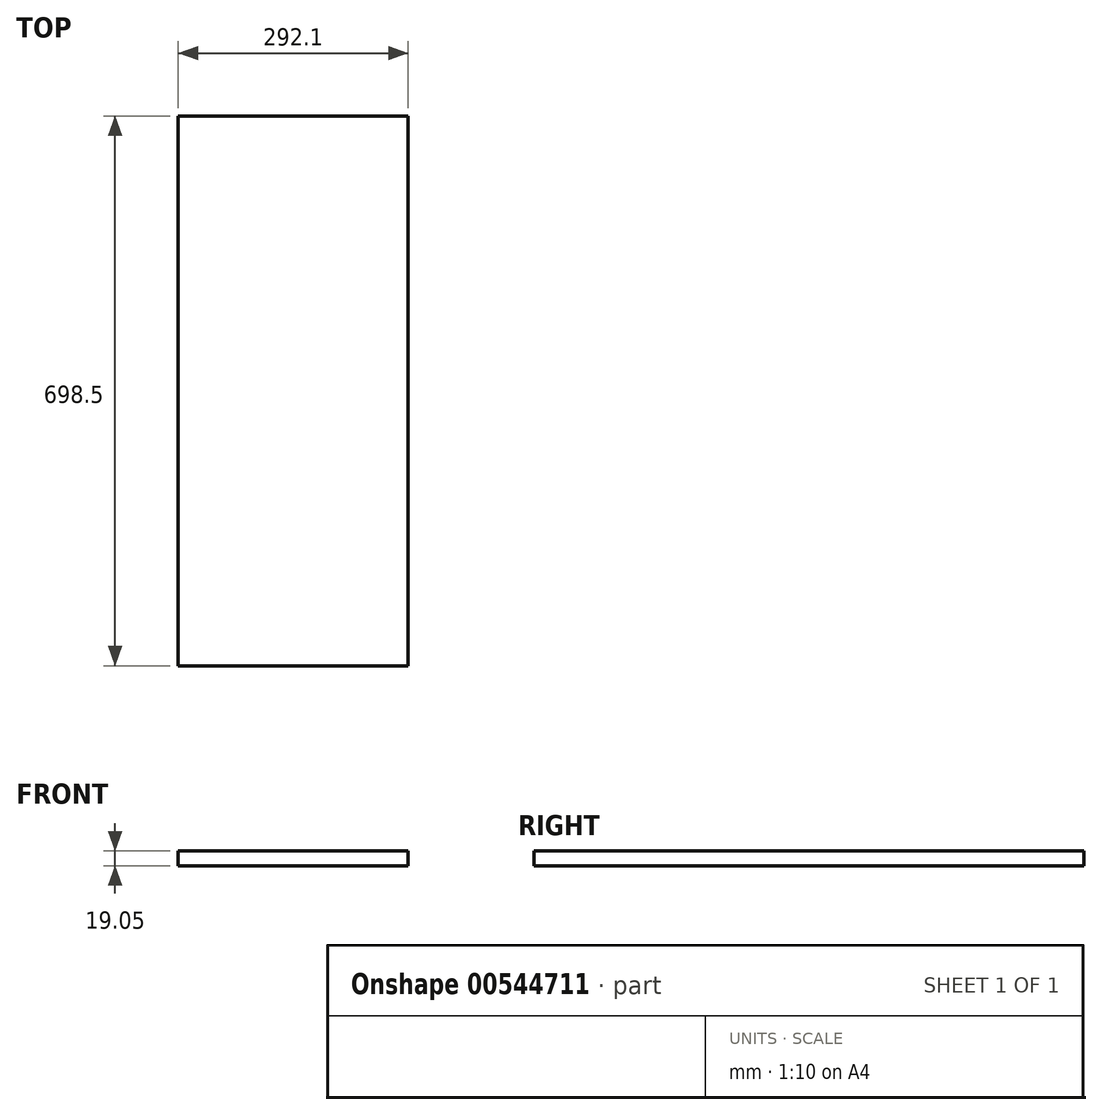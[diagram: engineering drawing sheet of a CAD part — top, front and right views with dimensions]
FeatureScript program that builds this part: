
annotation { "Feature Type Name" : "Feature", "Feature Type Description" : "" }
export const myFeature = defineFeature(function(context is Context, id is Id, definition is map)
    precondition{}
    {
        {
            var Q0;
            Q0=qCreatedBy(makeId("Top.planeOp"),FACE);
            var sketch = newSketch(context, id + "F0", { "sketchPlane" : qUnion([Q0])});
            skLineSegment(sketch, "E0.bottom", {"start": v(0, 0) * mm, "end": v(292.1, 0) * mm});
            skLineSegment(sketch, "E0.top", {"start": v(0, 698.5) * mm, "end": v(292.1, 698.5) * mm});
            skLineSegment(sketch, "E0.left", {"start": v(0, 0) * mm, "end": v(0, 698.5) * mm});
            skLineSegment(sketch, "E0.right", {"start": v(292.1, 0) * mm, "end": v(292.1, 698.5) * mm});
            skSolve(sketch);
        }
        {
            var Q0;
            Q0=makeQuery(id+"F0.imprint","IMPRINT",FACE,{"disambiguationData":[TD([[makeQuery(id+"F0.imprint","IMPRINT",EDGE,{"derivedFrom":sQuery(id+"F0.wireOp",EDGE,"E0.bottom")}),1.0]])]});
            extrude(context, id + "F1", {"entities" : qUnion([Q0]), "depth" : 19.05 * mm, "offsetDistance" : 25.4 * mm});
        }
    });
